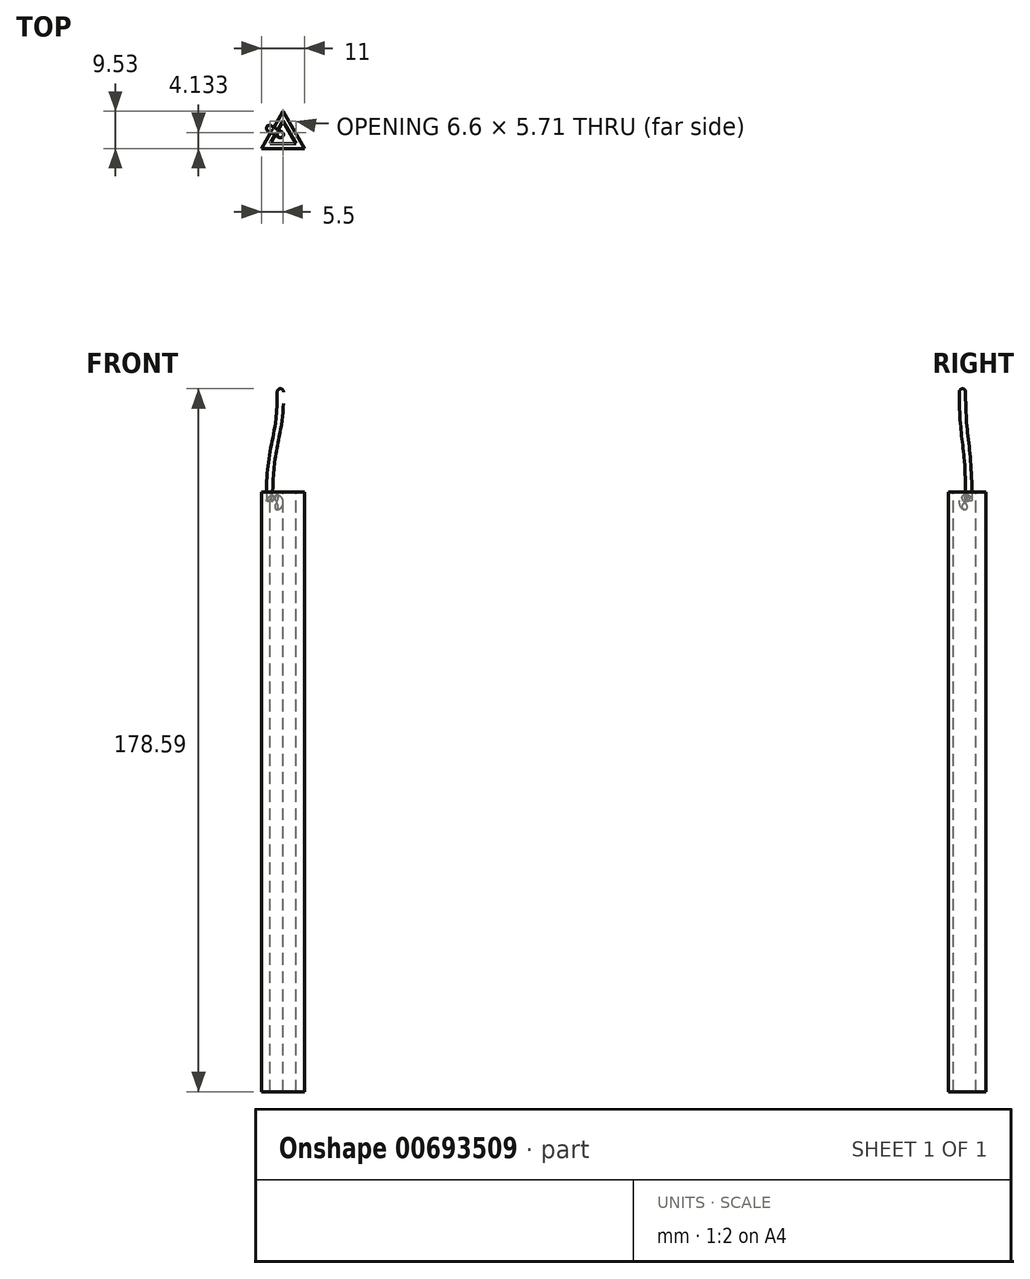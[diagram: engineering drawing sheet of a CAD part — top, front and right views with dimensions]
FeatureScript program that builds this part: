
annotation { "Feature Type Name" : "Feature", "Feature Type Description" : "" }
export const myFeature = defineFeature(function(context is Context, id is Id, definition is map)
    precondition{}
    {
        {
            var Q0;
            Q0=qCreatedBy(makeId("Top.planeOp"),FACE);
            var sketch = newSketch(context, id + "F0", { "sketchPlane" : qUnion([Q0])});
            skCircle(sketch, "E0", {"center": v(0, 0) * mm, "radius": 6.35 * mm});
            skCircle(sketch, "E1.cCircle", {"center": v(0, 0) * mm, "radius": 6.35 * mm, "construction": true});
            skLineSegment(sketch, "E1.0", {"start": v(0, 6.35) * mm, "end": v(5.5, -3.17) * mm});
            skLineSegment(sketch, "E1.1", {"start": v(5.5, -3.17) * mm, "end": v(-5.5, -3.18) * mm});
            skLineSegment(sketch, "E1.2", {"start": v(-5.5, -3.18) * mm, "end": v(0, 6.35) * mm});
            skLineSegment(sketch, "E2", {"start": v(5.5, -3.18) * mm, "end": v(-2.75, 1.59) * mm});
            skLineSegment(sketch, "E3", {"start": v(-5.5, -3.18) * mm, "end": v(2.75, 1.59) * mm});
            skLineSegment(sketch, "E4", {"start": v(0, -3.18) * mm, "end": v(0, 6.35) * mm});
            skLineSegment(sketch, "E5.0", {"start": v(-3.3, -1.9) * mm, "end": v(0, 3.8) * mm});
            skLineSegment(sketch, "E5.1", {"start": v(3.3, -1.9) * mm, "end": v(-3.3, -1.9) * mm});
            skLineSegment(sketch, "E5.2", {"start": v(0, 3.8) * mm, "end": v(3.3, -1.9) * mm});
            skPoint(sketch, "E6", {"position": v(-1.65, 0.95) * mm});
            skPoint(sketch, "E6.positionSnap0", {"position": v(-1.65, 0.95) * mm});
            skPoint(sketch, "E7", {"position": v(1.65, 0.95) * mm});
            skLineSegment(sketch, "E8", {"start": v(-2.75, 1.59) * mm, "end": v(-5.5, 3.17) * mm});
            skLineSegment(sketch, "E9", {"start": v(2.75, 1.59) * mm, "end": v(5.5, 3.18) * mm});
            skSolve(sketch);
        }
        {
            var Q0;
            Q0=qCreatedBy(makeId("Front.planeOp"),FACE);
            var sketch = newSketch(context, id + "F1", { "sketchPlane" : qUnion([Q0])});
            skLineSegment(sketch, "E10", {"start": v(0, 0) * mm, "end": v(0, 25.4) * mm});
            skSolve(sketch);
        }
        {
            var Q0;
            Q0=sQuery(id+"F0.wireOp",VERTEX,"E2.end");
            var Q1;
            Q1=sQuery(id+"F1.wireOp",VERTEX,"E10.end");
            var Q2;
            Q2=sQuery(id+"F0.wireOp",VERTEX,"E1.0.end");
            cPlane(context, id + "F2", {"entities" : qUnion([Q0, Q1, Q2]), "cplaneType" : CPlaneType.THREE_POINT, "offset" : 25.4 * mm, "width" : 152.4 * mm, "height" : 152.4 * mm});
        }
        {
            var Q0;
            Q0=qCreatedBy(id+"F2.planeOp",FACE);
            var sketch = newSketch(context, id + "F3", { "sketchPlane" : qUnion([Q0])});
            skLineSegment(sketch, "E11", {"start": v(-6.35, 0) * mm, "end": v(-6.35, 4.76) * mm});
            skLineSegment(sketch, "E12", {"start": v(0, 0) * mm, "end": v(0, 25.4) * mm});
            skLineSegment(sketch, "E13", {"start": v(-3.17, 0) * mm, "end": v(-3.17, -6.35) * mm});
            skLineSegment(sketch, "E14", {"start": v(-1.9, 0) * mm, "end": v(-1.9, -3.18) * mm});
            skPoint(sketch, "E15", {"position": v(0, 12.7) * mm});
            skLineSegment(sketch, "E16", {"start": v(-3.17, 0) * mm, "end": v(-3.17, 3.18) * mm});
            skPoint(sketch, "E17", {"position": v(-3.17, 0) * mm});
            skPoint(sketch, "E18", {"position": v(-1.9, -1.59) * mm});
            skLineSegment(sketch, "E19", {"start": v(-1.9, -1.59) * mm, "end": v(-1.9, -2.38) * mm});
            skPoint(sketch, "E20", {"position": v(-3.17, -1.59) * mm});
            skPoint(sketch, "E21", {"position": v(-3.17, -2.38) * mm});
            skPoint(sketch, "E22", {"position": v(-3.17, -3.18) * mm});
            skLineSegment(sketch, "E23", {"start": v(-1.9, -3.18) * mm, "end": v(-1.9, -6.35) * mm});
            skSolve(sketch);
        }
        {
            var Q0;
            Q0=sQuery(id+"F0.wireOp",VERTEX,"E3.start");
            var Q1;
            Q1=sQuery(id+"F0.wireOp",VERTEX,"E3.end");
            var Q2;
            Q2=sQuery(id+"F1.wireOp",VERTEX,"E10.end");
            cPlane(context, id + "F4", {"entities" : qUnion([Q0, Q1, Q2]), "cplaneType" : CPlaneType.THREE_POINT, "offset" : 25.4 * mm, "width" : 152.4 * mm, "height" : 152.4 * mm});
        }
        {
            var Q0;
            Q0=qCreatedBy(id+"F4.planeOp",FACE);
            var sketch = newSketch(context, id + "F5", { "sketchPlane" : qUnion([Q0])});
            skLineSegment(sketch, "E24", {"start": v(-6.35, 0) * mm, "end": v(-6.35, 3.18) * mm});
            skLineSegment(sketch, "E25", {"start": v(-1.9, 0) * mm, "end": v(-1.9, -3.18) * mm});
            skLineSegment(sketch, "E26", {"start": v(-3.17, 0) * mm, "end": v(-3.17, -6.35) * mm});
            skLineSegment(sketch, "E27", {"start": v(-3.17, 0) * mm, "end": v(-3.17, 1.59) * mm});
            skSolve(sketch);
        }
        {
            var Q0;
            Q0=qCreatedBy(id+"F4.planeOp",FACE);
            var sketch = newSketch(context, id + "F6", { "sketchPlane" : qUnion([Q0])});
            skLineSegment(sketch, "E28", {"start": v(0, 25.4) * mm, "end": v(0, 12.7) * mm});
            skArc(sketch, "E29", {"start": v(-6.35, 3.18) * mm, "mid": v(-1.62, 13.84) * mm, "end": v(0, 25.4) * mm});
            skLineSegment(sketch, "E30", {"start": v(-3.17, -6.35) * mm, "end": v(-3.17, 1.59) * mm});
            skArc(sketch, "E31", {"start": v(0, 12.7) * mm, "mid": v(-2.37, 7.37) * mm, "end": v(-3.18, 1.59) * mm});
            skArc(sketch, "E32", {"start": v(-6.35, 3.17) * mm, "mid": v(-5.54, -1.85) * mm, "end": v(-3.18, -6.35) * mm});
            skSolve(sketch);
        }
        {
            var Q0;
            Q0=qCreatedBy(makeId("Top.planeOp"),FACE);
            var sketch = newSketch(context, id + "F7", { "sketchPlane" : qUnion([Q0])});
            skLineSegment(sketch, "E33.0", {"start": v(0, 6.35) * mm, "end": v(5.5, -3.17) * mm});
            skLineSegment(sketch, "E33.1", {"start": v(5.5, -3.17) * mm, "end": v(-5.5, -3.18) * mm});
            skLineSegment(sketch, "E33.2", {"start": v(-5.5, -3.18) * mm, "end": v(0, 6.35) * mm});
            skLineSegment(sketch, "E34.0", {"start": v(-3.3, -1.9) * mm, "end": v(0, 3.8) * mm});
            skLineSegment(sketch, "E34.1", {"start": v(3.3, -1.9) * mm, "end": v(-3.3, -1.9) * mm});
            skLineSegment(sketch, "E34.2", {"start": v(0, 3.8) * mm, "end": v(3.3, -1.9) * mm});
            skPoint(sketch, "E35", {"position": v(-1.65, 0.95) * mm});
            skPoint(sketch, "E35.positionSnap0", {"position": v(-1.65, 0.95) * mm});
            skPoint(sketch, "E36", {"position": v(1.65, 0.95) * mm});
            skPoint(sketch, "E37.center.orphan", {"position": v(0, 0) * mm});
            skPoint(sketch, "E38.start.orphan", {"position": v(0, -3.17) * mm});
            skPoint(sketch, "E39.start.orphan", {"position": v(2.75, 1.59) * mm});
            skPoint(sketch, "E40.start.orphan", {"position": v(-2.75, 1.59) * mm});
            skSolve(sketch);
        }
        {
            var Q0;
            Q0=makeQuery(id+"F7.imprint","IMPRINT",FACE,{"disambiguationData":[TD([[makeQuery(id+"F7.imprint","IMPRINT",EDGE,{"derivedFrom":sQuery(id+"F7.wireOp",EDGE,"E33.0")}),-1.0]])]});
            extrude(context, id + "F8", {"entities" : qUnion([Q0]), "oppositeDirection" : true, "depth" : 152.4 * mm, "offsetDistance" : 25.4 * mm});
        }
        {
            var Q0;
            Q0=makeQuery(id+"F8.opExtrude","CAP_VERTEX",VERTEX,{"disambiguationData":[OSD([sQuery(id+"F7.wireOp",EDGE,"E33.0"),sQuery(id+"F7.wireOp",EDGE,"E33.2")])],"isStart":true});
            var Q1;
            Q1=makeQuery(id+"F8.opExtrude","CAP_VERTEX",VERTEX,{"disambiguationData":[OSD([sQuery(id+"F7.wireOp",EDGE,"E33.1"),sQuery(id+"F7.wireOp",EDGE,"E33.2")])],"isStart":true});
            var Q2;
            Q2=makeQuery(id+"F8.opExtrude","CAP_VERTEX",VERTEX,{"disambiguationData":[OSD([sQuery(id+"F7.wireOp",EDGE,"E33.0"),sQuery(id+"F7.wireOp",EDGE,"E33.2")])],"isStart":false});
            cPlane(context, id + "F9", {"entities" : qUnion([Q0, Q1, Q2]), "cplaneType" : CPlaneType.THREE_POINT, "offset" : 25.4 * mm, "width" : 152.4 * mm, "height" : 152.4 * mm});
        }
        {
            var Q0;
            Q0=qCreatedBy(id+"F9.planeOp",FACE);
            var sketch = newSketch(context, id + "F10", { "sketchPlane" : qUnion([Q0])});
            skLineSegment(sketch, "E41", {"start": v(0, 0) * mm, "end": v(0, -1.59) * mm});
            skPoint(sketch, "E42", {"position": v(0, -0.8) * mm});
            skCircle(sketch, "E43", {"center": v(0, -1.59) * mm, "radius": 0.8 * mm});
            skSolve(sketch);
        }
        {
            var Q0;
            Q0=makeQuery(id+"F10.imprint","IMPRINT",FACE,{"disambiguationData":[TD([[makeQuery(id+"F10.imprint","IMPRINT",EDGE,{"derivedFrom":sQuery(id+"F10.wireOp",EDGE,"E43")}),1.0]])]});
            extrude(context, id + "F11", {"entities" : qUnion([Q0]), "operationType" : NewBodyOperationType.REMOVE, "oppositeDirection" : true, "depth" : 1.27 * mm, "offsetDistance" : 25.4 * mm});
        }
        {
            var Q0;
            Q0=qCreatedBy(id+"F2.planeOp",FACE);
            var sketch = newSketch(context, id + "F12", { "sketchPlane" : qUnion([Q0])});
            skLineSegment(sketch, "E44", {"start": v(-3.97, -1.59) * mm, "end": v(-1.9, -1.59) * mm});
            skArc(sketch, "E45", {"start": v(-1.9, -1.59) * mm, "mid": v(-0.88, -2.7) * mm, "end": v(-1.96, -3.75) * mm});
            skPoint(sketch, "E46.start.orphan", {"position": v(-0.8, 25.4) * mm});
            skFitSpline(sketch, "E47", {"points": [v(-0.8, 25.4) * mm, v(-3.97, -1.59) * mm], "startDerivative": vector(0, -38.1) * mm, "endDerivative": vector(0, -42.86) * mm});
            skSolve(sketch);
        }
        {
            var Q0;
            Q0=qCreatedBy(makeId("Top.planeOp"),FACE);
            cPlane(context, id + "F13", {"entities" : qUnion([Q0]), "cplaneType" : CPlaneType.OFFSET, "offset" : 25.4 * mm, "width" : 152.4 * mm, "height" : 152.4 * mm});
        }
        {
            var Q0;
            Q0=qCreatedBy(id+"F13.planeOp",FACE);
            var sketch = newSketch(context, id + "F14", { "sketchPlane" : qUnion([Q0])});
            skCircle(sketch, "E48", {"center": v(-0.69, 0.4) * mm, "radius": 0.8 * mm});
            skLineSegment(sketch, "E49", {"start": v(-0.69, -0.4) * mm, "end": v(-0.69, 1.2) * mm});
            skSolve(sketch);
        }
        {
            var Q0;
            Q0=makeQuery(id+"F14.imprint","IMPRINT",FACE,{"disambiguationData":[TD([[makeQuery(id+"F14.imprint","IMPRINT",EDGE,{"derivedFrom":sQuery(id+"F14.wireOp",EDGE,"E48")}),1.0]])]});
            var Q1;
            Q1=sQuery(id+"F12.wireOp",EDGE,"E47");
            var Q2;
            Q2=sQuery(id+"F12.wireOp",EDGE,"E44");
            var Q3;
            Q3=sQuery(id+"F12.wireOp",EDGE,"E45");
            sweep(context, id + "F15", {"operationType" : NewBodyOperationType.ADD, "profiles" : qUnion([Q0]), "path" : qUnion([Q1, Q2, Q3])});
        }
        {
            var Q0;
            {var subQ0=sQuery(id+"F14.wireOp",EDGE,"E49");Q0=makeQuery(id+"F14.imprint","IMPRINT",FACE,{"disambiguationData":[TD([[makeQuery(id+"F14.imprint","IMPRINT",EDGE,{"derivedFrom":subQ0}),1.0]])]});}
            var Q1;
            Q1=sQuery(id+"F14.wireOp",EDGE,"E49");
            revolve(context, id + "F16", {"operationType" : NewBodyOperationType.ADD, "entities" : qUnion([Q0]), "axis" : qUnion([Q1]), "revolveType" : RevolveType.FULL});
        }
    });
